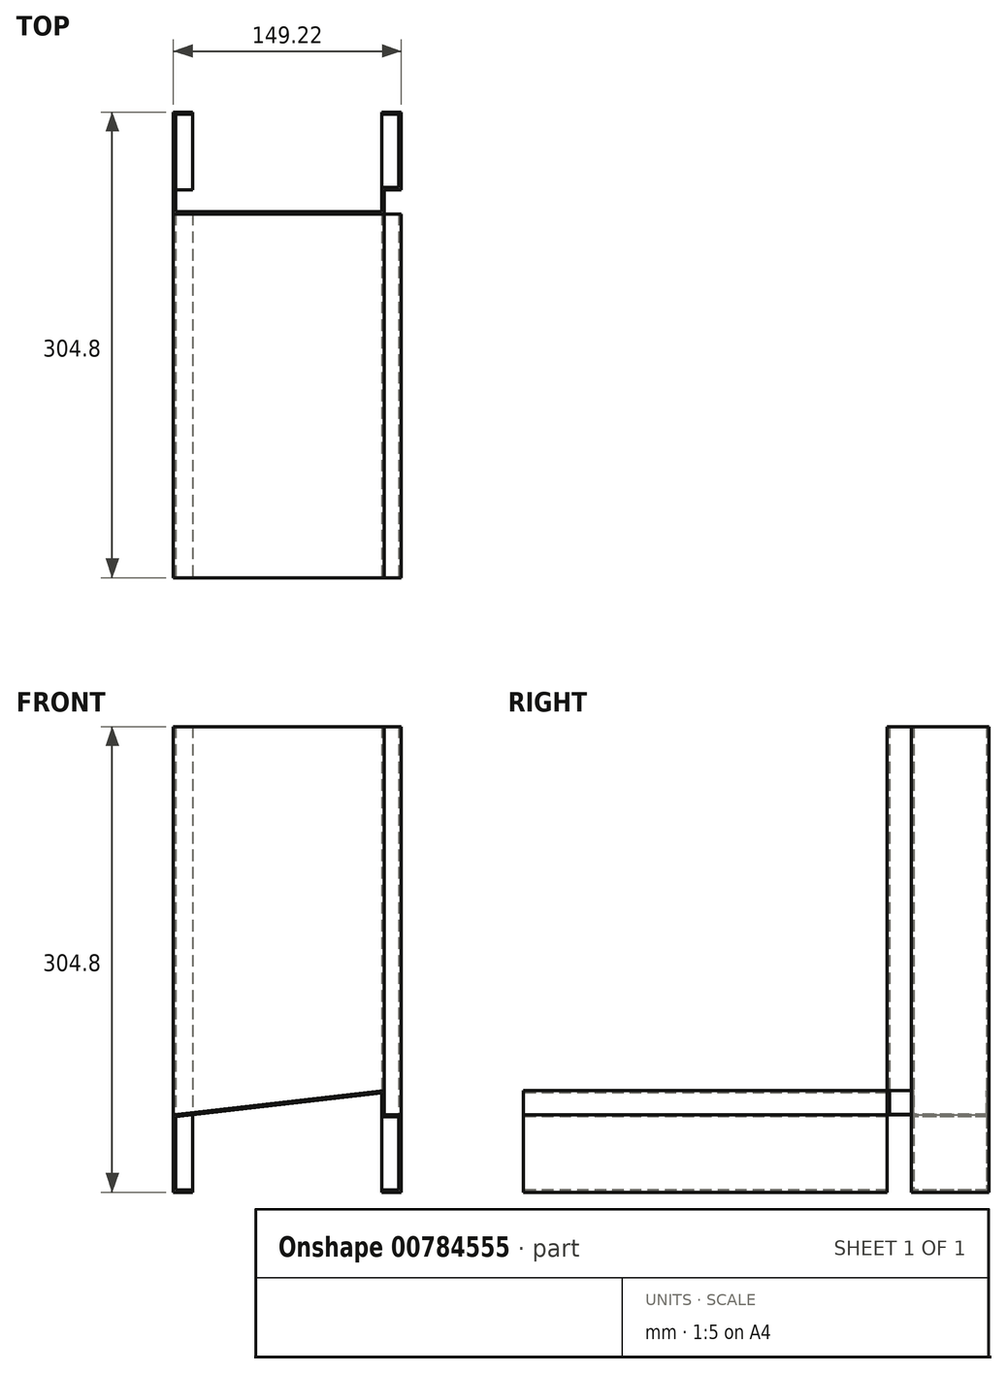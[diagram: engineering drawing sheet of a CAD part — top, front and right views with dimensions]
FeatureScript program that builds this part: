
annotation { "Feature Type Name" : "Feature", "Feature Type Description" : "" }
export const myFeature = defineFeature(function(context is Context, id is Id, definition is map)
    precondition{}
    {
        {
            var Q0;
            Q0=qCreatedBy(makeId("Front.planeOp"),FACE);
            var sketch = newSketch(context, id + "F0", { "sketchPlane" : qUnion([Q0])});
            skLineSegment(sketch, "E0", {"start": v(-61.91, -50.8) * mm, "end": v(-74.61, -50.8) * mm});
            skLineSegment(sketch, "E1", {"start": v(-74.61, -50.8) * mm, "end": v(-74.61, 0) * mm});
            skLineSegment(sketch, "E2", {"start": v(-74.61, 0) * mm, "end": v(63.5, 15.87) * mm});
            skLineSegment(sketch, "E3", {"start": v(63.5, 15.87) * mm, "end": v(63.5, 0) * mm});
            skLineSegment(sketch, "E4", {"start": v(63.5, 0) * mm, "end": v(74.61, 0) * mm});
            skLineSegment(sketch, "E5", {"start": v(74.61, 0) * mm, "end": v(74.61, -50.8) * mm});
            skLineSegment(sketch, "E6", {"start": v(74.61, -50.8) * mm, "end": v(61.91, -50.8) * mm});
            skLineSegment(sketch, "E7", {"start": v(-61.91, -50.8) * mm, "end": v(0, -50.8) * mm, "construction": true});
            skLineSegment(sketch, "E8", {"start": v(0, -50.8) * mm, "end": v(61.91, -50.8) * mm, "construction": true});
            skLineSegment(sketch, "E9.0", {"start": v(73.09, -49.28) * mm, "end": v(61.91, -49.28) * mm});
            skLineSegment(sketch, "E9.1", {"start": v(73.09, -1.52) * mm, "end": v(73.09, -49.28) * mm});
            skLineSegment(sketch, "E9.2", {"start": v(61.98, -1.52) * mm, "end": v(73.09, -1.52) * mm});
            skLineSegment(sketch, "E9.3", {"start": v(-61.91, -49.28) * mm, "end": v(-73.09, -49.28) * mm});
            skLineSegment(sketch, "E9.4", {"start": v(-73.09, -49.28) * mm, "end": v(-73.09, -1.36) * mm});
            skLineSegment(sketch, "E9.5", {"start": v(-73.09, -1.36) * mm, "end": v(61.98, 14.17) * mm});
            skLineSegment(sketch, "E9.6", {"start": v(61.98, 14.17) * mm, "end": v(61.98, -1.52) * mm});
            skLineSegment(sketch, "E10", {"start": v(-61.91, -49.28) * mm, "end": v(-61.91, -50.8) * mm});
            skLineSegment(sketch, "E11", {"start": v(61.91, -50.8) * mm, "end": v(61.91, -49.28) * mm});
            skSolve(sketch);
        }
        {
            var Q0;
            Q0=qSketchRegion(id+"F0",true);
            extrude(context, id + "F1", {"entities" : qUnion([Q0]), "oppositeDirection" : true, "depth" : 304.8 * mm, "offsetDistance" : 25.4 * mm});
        }
        {
            var Q0;
            Q0=qCreatedBy(makeId("Top.planeOp"),FACE);
            var sketch = newSketch(context, id + "F2", { "sketchPlane" : qUnion([Q0])});
            skPoint(sketch, "E12.0", {"position": v(-74.61, 304.8) * mm});
            skPoint(sketch, "E13.0", {"position": v(74.61, 304.8) * mm});
            skPoint(sketch, "E14.0", {"position": v(61.98, 304.8) * mm});
            skLineSegment(sketch, "E15", {"start": v(-74.61, 304.8) * mm, "end": v(-74.61, 238.12) * mm});
            skLineSegment(sketch, "E16", {"start": v(-74.61, 238.12) * mm, "end": v(63.5, 238.13) * mm});
            skLineSegment(sketch, "E17", {"start": v(63.5, 254) * mm, "end": v(74.61, 254) * mm});
            skLineSegment(sketch, "E18", {"start": v(74.61, 254) * mm, "end": v(74.61, 304.8) * mm});
            skLineSegment(sketch, "E19", {"start": v(61.98, 304.8) * mm, "end": v(74.61, 304.8) * mm});
            skLineSegment(sketch, "E20", {"start": v(-74.61, 304.8) * mm, "end": v(-61.91, 304.8) * mm});
            skLineSegment(sketch, "E21.0", {"start": v(-73.09, 303.28) * mm, "end": v(-61.91, 303.28) * mm});
            skLineSegment(sketch, "E21.1", {"start": v(-73.09, 303.28) * mm, "end": v(-73.09, 239.65) * mm});
            skLineSegment(sketch, "E21.2", {"start": v(-73.09, 239.65) * mm, "end": v(61.98, 239.65) * mm});
            skLineSegment(sketch, "E21.3", {"start": v(61.98, 303.28) * mm, "end": v(73.09, 303.28) * mm});
            skLineSegment(sketch, "E21.4", {"start": v(73.09, 255.52) * mm, "end": v(73.09, 303.28) * mm});
            skLineSegment(sketch, "E21.5", {"start": v(61.98, 255.52) * mm, "end": v(73.09, 255.52) * mm});
            skLineSegment(sketch, "E21.6", {"start": v(61.98, 239.65) * mm, "end": v(61.98, 255.52) * mm});
            skLineSegment(sketch, "E22", {"start": v(-61.91, 304.8) * mm, "end": v(-61.91, 303.28) * mm});
            skLineSegment(sketch, "E23", {"start": v(61.98, 304.8) * mm, "end": v(61.98, 303.28) * mm});
            skLineSegment(sketch, "E24", {"start": v(63.5, 238.13) * mm, "end": v(63.5, 254) * mm});
            skSolve(sketch);
        }
        {
            var Q0;
            Q0=qSketchRegion(id+"F2",true);
            extrude(context, id + "F3", {"entities" : qUnion([Q0]), "depth" : 254 * mm, "offsetDistance" : 25.4 * mm, "hasSecondDirection" : true, "secondDirectionOppositeDirection" : true, "secondDirectionDepth" : 50.8 * mm});
        }
        {
            var Q0;
            Q0=makeQuery(id+"F1.opExtrude","SWEPT_BODY",BODY,{"disambiguationData":[OSD([sQuery(id+"F0.wireOp",EDGE,"E0"),sQuery(id+"F0.wireOp",EDGE,"E1"),sQuery(id+"F0.wireOp",EDGE,"E2"),sQuery(id+"F0.wireOp",EDGE,"E3"),sQuery(id+"F0.wireOp",EDGE,"E4"),sQuery(id+"F0.wireOp",EDGE,"E5"),sQuery(id+"F0.wireOp",EDGE,"E6"),sQuery(id+"F0.wireOp",EDGE,"E9.0"),sQuery(id+"F0.wireOp",EDGE,"E9.1"),sQuery(id+"F0.wireOp",EDGE,"E9.2"),sQuery(id+"F0.wireOp",EDGE,"E9.3"),sQuery(id+"F0.wireOp",EDGE,"E9.4"),sQuery(id+"F0.wireOp",EDGE,"E9.5"),sQuery(id+"F0.wireOp",EDGE,"E9.6"),sQuery(id+"F0.wireOp",EDGE,"E10"),sQuery(id+"F0.wireOp",EDGE,"E11")])]});
            var Q1;
            Q1=makeQuery(id+"F3.opExtrude","SWEPT_BODY",BODY,{"disambiguationData":[OSD([sQuery(id+"F2.wireOp",EDGE,"E15"),sQuery(id+"F2.wireOp",EDGE,"E16"),sQuery(id+"F2.wireOp",EDGE,"vNE0MKmX-Wy9i-YOhV-lQRx-KuhJFtJfketY"),sQuery(id+"F2.wireOp",EDGE,"E17"),sQuery(id+"F2.wireOp",EDGE,"E18"),sQuery(id+"F2.wireOp",EDGE,"E19"),sQuery(id+"F2.wireOp",EDGE,"E20"),sQuery(id+"F2.wireOp",EDGE,"E21.0"),sQuery(id+"F2.wireOp",EDGE,"E21.1"),sQuery(id+"F2.wireOp",EDGE,"E21.2"),sQuery(id+"F2.wireOp",EDGE,"E21.3"),sQuery(id+"F2.wireOp",EDGE,"E21.4"),sQuery(id+"F2.wireOp",EDGE,"E21.5"),sQuery(id+"F2.wireOp",EDGE,"E21.6"),sQuery(id+"F2.wireOp",EDGE,"E22"),sQuery(id+"F2.wireOp",EDGE,"E23")])]});
            booleanBodies(context, id + "F4", {"operationType" : BooleanOperationType.INTERSECTION, "tools" : qUnion([Q0, Q1]), "keepTools" : true});
        }
        {
            var Q0;
            Q0=makeQuery(id+"F3.opExtrude","SWEPT_FACE",FACE,{"disambiguationData":[OSD([sQuery(id+"F2.wireOp",EDGE,"E16")])]});
            var sketch = newSketch(context, id + "F5", { "sketchPlane" : qUnion([Q0])});
            skPoint(sketch, "E25.0", {"position": v(61.98, 14.17) * mm});
            skPoint(sketch, "E26.0", {"position": v(-73.09, -1.36) * mm});
            skLineSegment(sketch, "E27", {"start": v(-73.09, -1.36) * mm, "end": v(61.98, 14.17) * mm});
            skLineSegment(sketch, "E28", {"start": v(-73.09, -1.36) * mm, "end": v(-91.14, -3.43) * mm});
            skPoint(sketch, "E29.0", {"position": v(61.98, 0) * mm});
            skLineSegment(sketch, "E30", {"start": v(61.98, 14.17) * mm, "end": v(61.98, 0) * mm});
            skLineSegment(sketch, "E31", {"start": v(61.98, 0) * mm, "end": v(86.32, 0) * mm});
            skLineSegment(sketch, "E32", {"start": v(-91.14, -3.43) * mm, "end": v(-91.14, -71.1) * mm});
            skLineSegment(sketch, "E33", {"start": v(-91.14, -71.1) * mm, "end": v(86.32, -71.1) * mm});
            skLineSegment(sketch, "E34", {"start": v(86.32, -71.1) * mm, "end": v(86.32, 0) * mm});
            skPoint(sketch, "E35.0", {"position": v(63.5, 0) * mm});
            skSolve(sketch);
        }
        {
            var Q0;
            Q0 = qSketchRegion(id + "F5", true);
            var Q1;
            Q1=makeQuery(id+"F3.opExtrude","SWEPT_FACE",FACE,{"disambiguationData":[OSD([sQuery(id+"F2.wireOp",EDGE,"E17")])]});
            extrude(context, id + "F6", {"entities" : qUnion([Q0]), "operationType" : NewBodyOperationType.REMOVE, "endBound" : BoundingType.UP_TO_SURFACE, "oppositeDirection" : true, "depth" : 25.4 * mm, "endBoundEntityFace" : qUnion([Q1]), "offsetDistance" : 25.4 * mm});
        }
        {
            var Q0;
            Q0=makeQuery(id+"F3.opExtrude","SWEPT_FACE",FACE,{"disambiguationData":[OSD([sQuery(id+"F2.wireOp",EDGE,"E16")])]});
            var sketch = newSketch(context, id + "F7", { "sketchPlane" : qUnion([Q0])});
            skPoint(sketch, "E36.0", {"position": v(-74.61, -1.53) * mm});
            skPoint(sketch, "E37.0", {"position": v(63.5, 0) * mm});
            skPoint(sketch, "E38.0", {"position": v(61.98, 0) * mm});
            skPoint(sketch, "E39.0", {"position": v(63.5, 15.87) * mm});
            skPoint(sketch, "E40.0", {"position": v(-74.61, 0) * mm});
            skPoint(sketch, "E41.0", {"position": v(-73.09, -1.36) * mm});
            skPoint(sketch, "E42.0", {"position": v(61.98, 14.17) * mm});
            skLineSegment(sketch, "E43", {"start": v(-74.61, -1.53) * mm, "end": v(61.98, 14.17) * mm});
            skLineSegment(sketch, "E44", {"start": v(61.98, 14.17) * mm, "end": v(61.98, 0) * mm});
            skLineSegment(sketch, "E45", {"start": v(61.98, 0) * mm, "end": v(63.5, 0) * mm});
            skLineSegment(sketch, "E46", {"start": v(63.5, 0) * mm, "end": v(63.5, 15.87) * mm});
            skLineSegment(sketch, "E47", {"start": v(63.5, 15.87) * mm, "end": v(-74.61, 0) * mm});
            skLineSegment(sketch, "E48", {"start": v(-74.61, 0) * mm, "end": v(-74.61, -1.53) * mm});
            skSolve(sketch);
        }
        {
            var Q0;
            Q0 = qSketchRegion(id + "F7", true);
            extrude(context, id + "F8", {"entities" : qUnion([Q0]), "operationType" : NewBodyOperationType.REMOVE, "endBound" : BoundingType.THROUGH_ALL, "oppositeDirection" : true, "depth" : 25.4 * mm, "offsetDistance" : 25.4 * mm});
        }
        {
            var Q0;
            Q0=makeQuery(id+"F4.opBoolean","INTERSECT",BODY,{"derivedFrom":[makeQuery(id+"F1.opExtrude","SWEPT_BODY",BODY,{"disambiguationData":[OSD([sQuery(id+"F0.wireOp",EDGE,"E0"),sQuery(id+"F0.wireOp",EDGE,"E1"),sQuery(id+"F0.wireOp",EDGE,"E2"),sQuery(id+"F0.wireOp",EDGE,"E3"),sQuery(id+"F0.wireOp",EDGE,"E4"),sQuery(id+"F0.wireOp",EDGE,"E5"),sQuery(id+"F0.wireOp",EDGE,"E6"),sQuery(id+"F0.wireOp",EDGE,"E9.0"),sQuery(id+"F0.wireOp",EDGE,"E9.1"),sQuery(id+"F0.wireOp",EDGE,"E9.2"),sQuery(id+"F0.wireOp",EDGE,"E9.3"),sQuery(id+"F0.wireOp",EDGE,"E9.4"),sQuery(id+"F0.wireOp",EDGE,"E9.5"),sQuery(id+"F0.wireOp",EDGE,"E9.6"),sQuery(id+"F0.wireOp",EDGE,"E10"),sQuery(id+"F0.wireOp",EDGE,"E11")])]}),makeQuery(id+"F3.opExtrude","SWEPT_BODY",BODY,{"disambiguationData":[OSD([sQuery(id+"F2.wireOp",EDGE,"E15"),sQuery(id+"F2.wireOp",EDGE,"E16"),sQuery(id+"F2.wireOp",EDGE,"E17"),sQuery(id+"F2.wireOp",EDGE,"E18"),sQuery(id+"F2.wireOp",EDGE,"E19"),sQuery(id+"F2.wireOp",EDGE,"E20"),sQuery(id+"F2.wireOp",EDGE,"E21.0"),sQuery(id+"F2.wireOp",EDGE,"E21.1"),sQuery(id+"F2.wireOp",EDGE,"E21.2"),sQuery(id+"F2.wireOp",EDGE,"E21.3"),sQuery(id+"F2.wireOp",EDGE,"E21.4"),sQuery(id+"F2.wireOp",EDGE,"E21.5"),sQuery(id+"F2.wireOp",EDGE,"E21.6"),sQuery(id+"F2.wireOp",EDGE,"E22"),sQuery(id+"F2.wireOp",EDGE,"E23"),sQuery(id+"F2.wireOp",EDGE,"E24")])]})]});
            deleteBodies(context, id + "F9", {"entities" : qUnion([Q0])});
        }
        {
            var Q0;
            Q0=makeQuery(id+"F1.opExtrude","SWEPT_BODY",BODY,{"disambiguationData":[OSD([sQuery(id+"F0.wireOp",EDGE,"E0"),sQuery(id+"F0.wireOp",EDGE,"E1"),sQuery(id+"F0.wireOp",EDGE,"E2"),sQuery(id+"F0.wireOp",EDGE,"E3"),sQuery(id+"F0.wireOp",EDGE,"E4"),sQuery(id+"F0.wireOp",EDGE,"E5"),sQuery(id+"F0.wireOp",EDGE,"E6"),sQuery(id+"F0.wireOp",EDGE,"E9.0"),sQuery(id+"F0.wireOp",EDGE,"E9.1"),sQuery(id+"F0.wireOp",EDGE,"E9.2"),sQuery(id+"F0.wireOp",EDGE,"E9.3"),sQuery(id+"F0.wireOp",EDGE,"E9.4"),sQuery(id+"F0.wireOp",EDGE,"E9.5"),sQuery(id+"F0.wireOp",EDGE,"E9.6"),sQuery(id+"F0.wireOp",EDGE,"E10"),sQuery(id+"F0.wireOp",EDGE,"E11")])]});
            var Q1;
            Q1=makeQuery(id+"F3.opExtrude","SWEPT_BODY",BODY,{"disambiguationData":[OSD([sQuery(id+"F2.wireOp",EDGE,"E15"),sQuery(id+"F2.wireOp",EDGE,"E16"),sQuery(id+"F2.wireOp",EDGE,"E17"),sQuery(id+"F2.wireOp",EDGE,"E18"),sQuery(id+"F2.wireOp",EDGE,"E19"),sQuery(id+"F2.wireOp",EDGE,"E20"),sQuery(id+"F2.wireOp",EDGE,"E21.0"),sQuery(id+"F2.wireOp",EDGE,"E21.1"),sQuery(id+"F2.wireOp",EDGE,"E21.2"),sQuery(id+"F2.wireOp",EDGE,"E21.3"),sQuery(id+"F2.wireOp",EDGE,"E21.4"),sQuery(id+"F2.wireOp",EDGE,"E21.5"),sQuery(id+"F2.wireOp",EDGE,"E21.6"),sQuery(id+"F2.wireOp",EDGE,"E22"),sQuery(id+"F2.wireOp",EDGE,"E23"),sQuery(id+"F2.wireOp",EDGE,"E24")])]});
            booleanBodies(context, id + "F10", {"operationType" : BooleanOperationType.UNION, "tools" : qUnion([Q0, Q1])});
        }
        {
            var Q0;
            {var subQ0=sQuery(id+"F0.wireOp",EDGE,"E3");var subQ2=sQuery(id+"F0.wireOp",EDGE,"E4");Q0=makeQuery(id+"F10.opBoolean","SPLIT",FACE,{"disambiguationData":[TD([makeQuery(id+"F1.opExtrude","SWEPT_FACE",FACE,{"disambiguationData":[OSD([subQ0])]})])],"derivedFrom":makeQuery(id+"F8.boolean.opBoolean","MERGE",FACE,{"derivedFrom":[makeQuery(id+"F1.opExtrude","SWEPT_FACE",FACE,{"disambiguationData":[OSD([subQ2])]})],"fromTools":[makeQuery(id+"F8.opExtrude","SWEPT_FACE",FACE,{"disambiguationData":[OSD([sQuery(id+"F7.wireOp",EDGE,"E45")])]})]})});}
            var sketch = newSketch(context, id + "F11", { "sketchPlane" : qUnion([Q0])});
            skPoint(sketch, "E49.0", {"position": v(63.5, 238.13) * mm});
            skLineSegment(sketch, "E50.bottom", {"start": v(63.5, 238.13) * mm, "end": v(61.37, 238.13) * mm});
            skLineSegment(sketch, "E50.top", {"start": v(63.5, 238.07) * mm, "end": v(61.37, 238.07) * mm});
            skLineSegment(sketch, "E50.left", {"start": v(63.5, 238.13) * mm, "end": v(63.5, 238.07) * mm});
            skLineSegment(sketch, "E50.right", {"start": v(61.37, 238.13) * mm, "end": v(61.37, 238.07) * mm});
            skSolve(sketch);
        }
        {
            var Q0;
            Q0 = qSketchRegion(id + "F11", true);
            extrude(context, id + "F12", {"entities" : qUnion([Q0]), "operationType" : NewBodyOperationType.REMOVE, "endBound" : BoundingType.THROUGH_ALL, "depth" : 25.4 * mm, "offsetDistance" : 25.4 * mm});
        }
    });
